# Revit family: Кольца стеновые с футеровкой анкерными листами V-Lock -ПБК ЭКОВЭЛЛ-
name_source: partatom
category: Обобщенные модели
revit_build: Autodesk Revit 2015 (Build: 20141119_1515(x64)
units: mm (PartAtom-declared; Revit-internal decimal feet)

## types (8) — shared parameters
Город и страна производства = Санкт-Петербург, Российская Федерация
Документ регламентирующий производство = ТУ 5855-001-23107031-2013
Изготовитель = ООО "ГИС"
Сайт изготовителя = http://gisspb.ru
Тип бетона = БСТ B20 П1 F200 W4 ГОСТ 7473-2010
Тип материалов покрытия = Полиэтилен низкого давления

## per-type parameters (varying)
| type | Внешний диаметр | Внутрений диаметр | Внутрений диаметр по футеровке | Высота | Масса | Толщина стенки |
| КС-20.9-ФУТ "ПБК ЭКОВЭЛЛ" с анкерными листами V-Lock | 2200 мм | 2000 мм | 1992 мм | 890 мм | 1516.00 kg | 100 мм |
| КС-20.6-ФУТ "ПБК ЭКОВЭЛЛ" с анкерными листами V-Lock | 2200 мм | 2000 мм | 1992 мм | 590 мм | 1004.00 kg | 100 мм |
| КС-15.9-ФУТ "ПБК ЭКОВЭЛЛ" с анкерными листами V-Lock | 1680 мм | 1500 мм | 1492 мм | 890 мм | 1027.00 kg | 90 мм |
| КС-15.6-ФУТ "ПБК ЭКОВЭЛЛ" с анкерными листами V-Lock | 1680 мм | 1500 мм | 1492 мм | 590 мм | 618.00 kg | 90 мм |
| КС-15.3-ФУТ "ПБК ЭКОВЭЛЛ" с анкерными листами V-Lock | 1680 мм | 1500 мм | 1492 мм | 290 мм | 412.00 kg | 90 мм |
| КС-10.9-ФУТ "ПБК ЭКОВЭЛЛ" с анкерными листами V-Lock | 1160 мм | 1000 мм | 992 мм | 890 мм | 618.00 kg | 80 мм |
| КС-10.6-ФУТ "ПБК ЭКОВЭЛЛ" с анкерными листами V-Lock | 1160 мм | 1000 мм | 992 мм | 590 мм | 412.00 kg | 80 мм |
| КС-10.3-ФУТ "ПБК ЭКОВЭЛЛ" с анкерными листами V-Lock | 1160 мм | 1000 мм | 992 мм | 290 мм | 206.00 kg | 80 мм |

## geometry (parser evidence)
native form markers: Blend x4
no freeform markers — native parametric forms only
